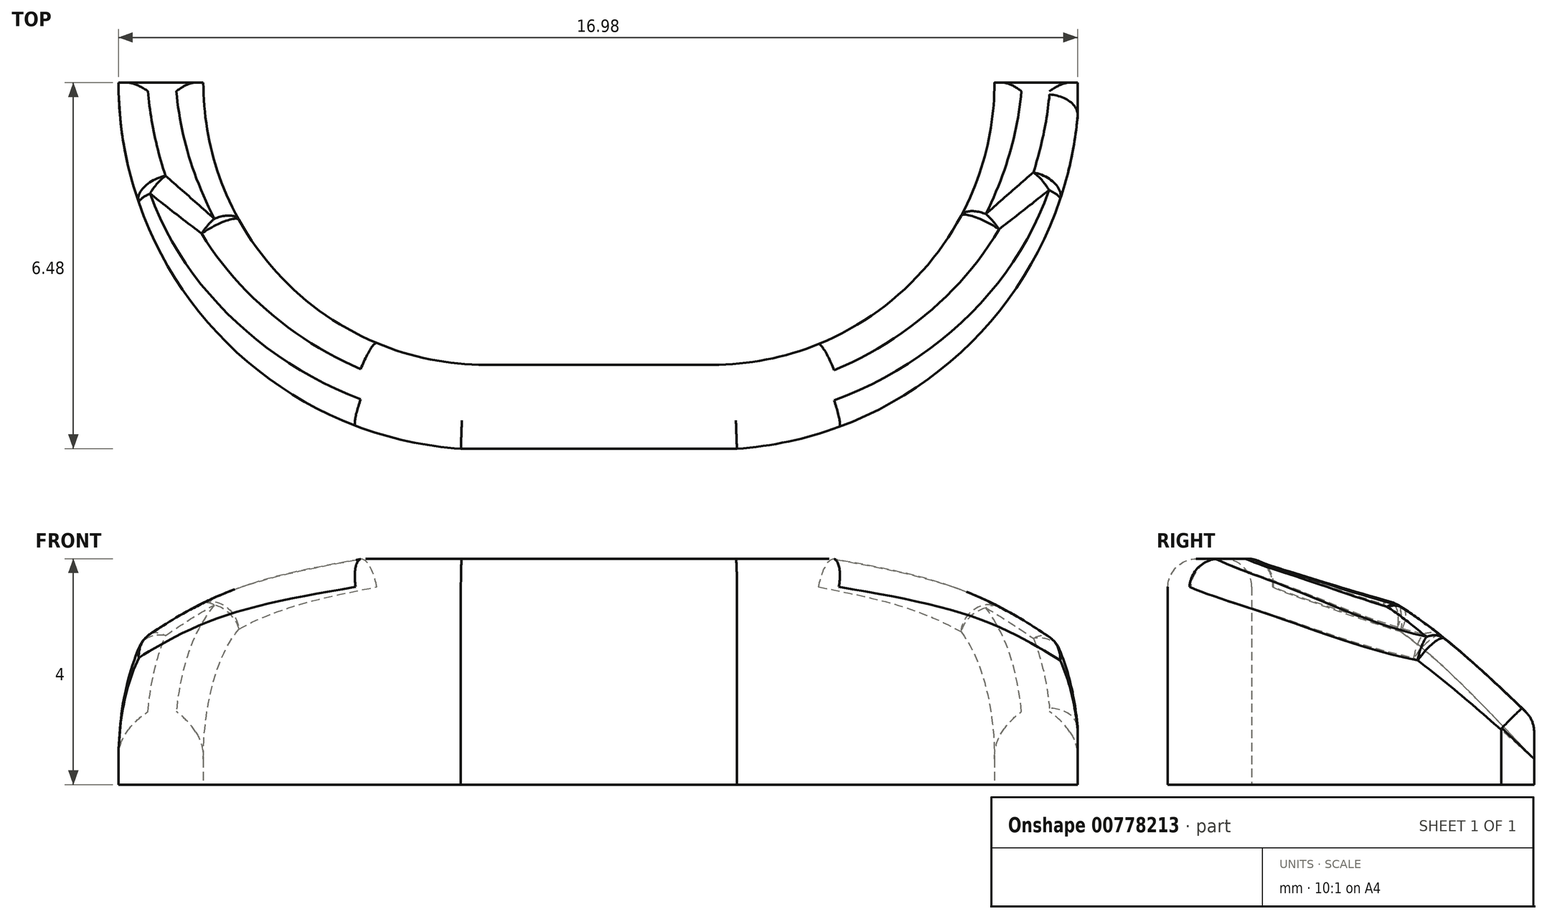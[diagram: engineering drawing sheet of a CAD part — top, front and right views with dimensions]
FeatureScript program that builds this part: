
annotation { "Feature Type Name" : "Feature", "Feature Type Description" : "" }
export const myFeature = defineFeature(function(context is Context, id is Id, definition is map)
    precondition{}
    {
        {
            var Q0;
            Q0=qCreatedBy(makeId("Top.planeOp"),FACE);
            var sketch = newSketch(context, id + "F0", { "sketchPlane" : qUnion([Q0])});
            skLineSegment(sketch, "E0", {"start": v(1.74, -7.18) * mm, "end": v(5.74, -7.18) * mm});
            skPoint(sketch, "E1.visualSharp", {"position": v(-3.26, -7.18) * mm});
            skArc(sketch, "E1.filletArc", {"start": v(-3.26, -2.18) * mm, "mid": v(-1.8, -5.72) * mm, "end": v(1.74, -7.18) * mm});
            skPoint(sketch, "E2.visualSharp", {"position": v(10.74, -7.18) * mm});
            skArc(sketch, "E2.filletArc", {"start": v(5.74, -7.18) * mm, "mid": v(9.28, -5.72) * mm, "end": v(10.74, -2.18) * mm});
            skArc(sketch, "E3.0", {"start": v(-4.76, -2.18) * mm, "mid": v(-2.86, -6.78) * mm, "end": v(1.74, -8.68) * mm});
            skArc(sketch, "E4.0", {"start": v(5.74, -8.68) * mm, "mid": v(10.34, -6.78) * mm, "end": v(12.24, -2.18) * mm});
            skLineSegment(sketch, "E5", {"start": v(1.74, -8.68) * mm, "end": v(5.74, -8.68) * mm});
            skLineSegment(sketch, "E6", {"start": v(-4.76, -2.18) * mm, "end": v(-3.26, -2.18) * mm});
            skLineSegment(sketch, "E7", {"start": v(10.74, -2.18) * mm, "end": v(12.24, -2.18) * mm});
            skPoint(sketch, "E8.start.orphan", {"position": v(-3.26, 0.61) * mm});
            skPoint(sketch, "E9.end.orphan", {"position": v(10.74, 0.61) * mm});
            skLineSegment(sketch, "E10", {"start": v(-4.76, -2.18) * mm, "end": v(-4.76, -8.68) * mm});
            skLineSegment(sketch, "E11", {"start": v(-4.76, -8.68) * mm, "end": v(12.24, -8.68) * mm});
            skLineSegment(sketch, "E12", {"start": v(12.24, -8.68) * mm, "end": v(12.24, -2.18) * mm});
            skLineSegment(sketch, "E13", {"start": v(12.24, -2.18) * mm, "end": v(-4.76, -2.18) * mm});
            skSolve(sketch);
        }
        {
            var Q0;
            Q0=makeQuery(id+"F0.imprint","IMPRINT",FACE,{"disambiguationData":[TD([[makeQuery(id+"F0.imprint","IMPRINT",EDGE,{"derivedFrom":sQuery(id+"F0.wireOp",EDGE,"E0")}),-1.0]])]});
            var Q1;
            Q1=makeQuery(id+"F0.imprint","IMPRINT",FACE,{"disambiguationData":[TD([[makeQuery(id+"F0.imprint","IMPRINT",EDGE,{"derivedFrom":sQuery(id+"F0.wireOp",EDGE,"E0")}),1.0]])]});
            var Q2;
            {var subQ0=sQuery(id+"F0.wireOp",EDGE,"E4.0");Q2=makeQuery(id+"F0.imprint","IMPRINT",FACE,{"disambiguationData":[TD([[makeQuery(id+"F0.imprint","IMPRINT",EDGE,{"derivedFrom":subQ0}),-1.0]])]});}
            var Q3;
            {var subQ0=sQuery(id+"F0.wireOp",EDGE,"E3.0");Q3=makeQuery(id+"F0.imprint","IMPRINT",FACE,{"disambiguationData":[TD([[makeQuery(id+"F0.imprint","IMPRINT",EDGE,{"derivedFrom":subQ0}),-1.0]])]});}
            extrude(context, id + "F1", {"entities" : qUnion([Q0, Q1, Q2, Q3]), "depth" : 4 * mm, "offsetDistance" : 25 * mm});
        }
        {
            var Q0;
            Q0=makeQuery(id+"F1.opExtrude","SWEPT_FACE",FACE,{"disambiguationData":[OSD([sQuery(id+"F0.wireOp",EDGE,"E12")])]});
            var sketch = newSketch(context, id + "F2", { "sketchPlane" : qUnion([Q0])});
            skFitSpline(sketch, "E14", {"points": [v(-6.61, 4) * mm, v(-4.66, 3.21) * mm, v(-2.18, 1.13) * mm], "startDerivative": vector(4.34, -1.32) * mm, "endDerivative": vector(4.51, -4.31) * mm});
            skSolve(sketch);
        }
        {
            var Q0;
            {var subQ0=sQuery(id+"F2.wireOp",EDGE,"E14");Q0=makeQuery(id+"F2.imprint","IMPRINT",FACE,{"disambiguationData":[TD([[makeQuery(id+"F2.imprint","IMPRINT",EDGE,{"derivedFrom":subQ0}),1.0]])]});}
            extrude(context, id + "F3", {"entities" : qUnion([Q0]), "operationType" : NewBodyOperationType.REMOVE, "endBound" : BoundingType.THROUGH_ALL, "oppositeDirection" : true, "depth" : 25 * mm, "offsetDistance" : 25 * mm});
        }
        {
            var Q0;
            Q0=makeQuery(id+"F1.opExtrude","SWEPT_FACE",FACE,{"disambiguationData":[OSD([sQuery(id+"F0.wireOp",EDGE,"E11")])]});
            var sketch = newSketch(context, id + "F4", { "sketchPlane" : qUnion([Q0])});
            skLineSegment(sketch, "E15", {"start": v(3.74, 4) * mm, "end": v(3.74, 0) * mm, "construction": true});
            skFitSpline(sketch, "E16", {"points": [v(-0.4, 4) * mm, v(-2.85, 3.4) * mm, v(-4.76, 2.27) * mm], "startDerivative": vector(-4.94, -0.89) * mm, "endDerivative": vector(-3.76, -2.59) * mm});
            skFitSpline(sketch, "E17.MirrorCS", {"points": [v(7.89, 4) * mm, v(10.33, 3.4) * mm, v(12.24, 2.27) * mm], "startDerivative": vector(4.94, -0.89) * mm, "endDerivative": vector(3.76, -2.59) * mm});
            skSolve(sketch);
        }
        {
            var Q0;
            {var subQ0=sQuery(id+"F4.wireOp",EDGE,"E16");Q0=makeQuery(id+"F4.imprint","IMPRINT",FACE,{"disambiguationData":[TD([[makeQuery(id+"F4.imprint","IMPRINT",EDGE,{"derivedFrom":subQ0}),-1.0]])]});}
            var Q1;
            {var subQ0=sQuery(id+"F4.wireOp",EDGE,"E17.MirrorCS");Q1=makeQuery(id+"F4.imprint","IMPRINT",FACE,{"disambiguationData":[TD([[makeQuery(id+"F4.imprint","IMPRINT",EDGE,{"derivedFrom":subQ0}),1.0]])]});}
            extrude(context, id + "F5", {"entities" : qUnion([Q0, Q1]), "operationType" : NewBodyOperationType.REMOVE, "endBound" : BoundingType.THROUGH_ALL, "oppositeDirection" : true, "depth" : 25 * mm, "offsetDistance" : 25 * mm});
        }
        {
            var Q0;
            Q0=makeQuery(id+"F1.opExtrude","CAP_FACE",FACE,{"disambiguationData":[OSD([sQuery(id+"F0.wireOp",EDGE,"E10"),sQuery(id+"F0.wireOp",EDGE,"E11"),sQuery(id+"F0.wireOp",EDGE,"E12"),sQuery(id+"F0.wireOp",EDGE,"E13")])],"isStart":true});
            var sketch = newSketch(context, id + "F6", { "sketchPlane" : qUnion([Q0])});
            skLineSegment(sketch, "E18", {"start": v(5.77, 7.2) * mm, "end": v(1.76, 7.2) * mm});
            skPoint(sketch, "E19.visualSharp", {"position": v(10.77, 7.2) * mm});
            skArc(sketch, "E19.filletArc", {"start": v(10.77, 2.2) * mm, "mid": v(9.3, 5.73) * mm, "end": v(5.77, 7.2) * mm});
            skPoint(sketch, "E20.visualSharp", {"position": v(-3.24, 7.2) * mm});
            skArc(sketch, "E20.filletArc", {"start": v(1.76, 7.2) * mm, "mid": v(-1.77, 5.73) * mm, "end": v(-3.24, 2.2) * mm});
            skArc(sketch, "E21.0", {"start": v(12.27, 2.2) * mm, "mid": v(10.36, 6.8) * mm, "end": v(5.77, 8.7) * mm});
            skArc(sketch, "E22.0", {"start": v(1.76, 8.7) * mm, "mid": v(-2.83, 6.8) * mm, "end": v(-4.74, 2.2) * mm});
            skLineSegment(sketch, "E23", {"start": v(5.77, 8.7) * mm, "end": v(1.76, 8.7) * mm});
            skLineSegment(sketch, "E24", {"start": v(12.27, 2.2) * mm, "end": v(10.77, 2.2) * mm});
            skLineSegment(sketch, "E25", {"start": v(-3.24, 2.2) * mm, "end": v(-4.74, 2.2) * mm});
            skSolve(sketch);
        }
        {
            var Q0;
            {var subQ0=sQuery(id+"F6.wireOp",EDGE,"E21.0");var subQ1=makeQuery(id+"F1.opExtrude","CAP_EDGE",EDGE,{"disambiguationData":[OSD([sQuery(id+"F0.wireOp",EDGE,"E12")])],"isStart":true});var subQ2=makeQuery(id+"F6.imprint","INTERSECT",VERTEX,{"derivedFrom":[subQ1,subQ0]});Q0=makeQuery(id+"F6.imprint","IMPRINT",FACE,{"disambiguationData":[TD([[makeQuery(id+"F6.imprint","IMPRINT",EDGE,{"disambiguationData":[TD([[subQ2,-1.0]])],"derivedFrom":subQ0}),-1.0]])]});}
            var Q1;
            Q1=makeQuery(id+"F6.imprint","IMPRINT",FACE,{"disambiguationData":[TD([[makeQuery(id+"F6.imprint","IMPRINT",EDGE,{"derivedFrom":sQuery(id+"F6.wireOp",EDGE,"E18")}),1.0]])]});
            extrude(context, id + "F7", {"entities" : qUnion([Q0, Q1]), "operationType" : NewBodyOperationType.REMOVE, "endBound" : BoundingType.THROUGH_ALL, "oppositeDirection" : true, "depth" : 25 * mm, "offsetDistance" : 25 * mm});
        }
        {
            var Q0;
            Q0=makeQuery(id+"F7.boolean.opBoolean","SPLIT",FACE,{"disambiguationData":[TD([makeQuery(id+"F5.boolean.opBoolean","COPY",FACE,{"derivedFrom":makeQuery(id+"F5.opExtrude","SWEPT_FACE",FACE,{"disambiguationData":[OSD([sQuery(id+"F4.wireOp",EDGE,"E16")])]})})])],"derivedFrom":makeQuery(id+"F3.boolean.opBoolean","COPY",FACE,{"derivedFrom":makeQuery(id+"F3.opExtrude","SWEPT_FACE",FACE,{"disambiguationData":[OSD([sQuery(id+"F2.wireOp",EDGE,"E14")])]})})});
            var Q1;
            Q1=makeQuery(id+"F7.boolean.opBoolean","SPLIT",FACE,{"disambiguationData":[TD([makeQuery(id+"F1.opExtrude","SWEPT_FACE",FACE,{"disambiguationData":[OSD([sQuery(id+"F0.wireOp",EDGE,"E12")])]})])],"derivedFrom":makeQuery(id+"F3.boolean.opBoolean","COPY",FACE,{"derivedFrom":makeQuery(id+"F3.opExtrude","SWEPT_FACE",FACE,{"disambiguationData":[OSD([sQuery(id+"F2.wireOp",EDGE,"E14")])]})})});
            var Q2;
            Q2=makeQuery(id+"F5.boolean.opBoolean","COPY",FACE,{"derivedFrom":makeQuery(id+"F5.opExtrude","SWEPT_FACE",FACE,{"disambiguationData":[OSD([sQuery(id+"F4.wireOp",EDGE,"E17.MirrorCS")])]})});
            var Q3;
            Q3=makeQuery(id+"F1.opExtrude","CAP_FACE",FACE,{"disambiguationData":[OSD([sQuery(id+"F0.wireOp",EDGE,"E10"),sQuery(id+"F0.wireOp",EDGE,"E11"),sQuery(id+"F0.wireOp",EDGE,"E12"),sQuery(id+"F0.wireOp",EDGE,"E13")])],"isStart":false});
            var Q4;
            Q4=makeQuery(id+"F5.boolean.opBoolean","COPY",FACE,{"derivedFrom":makeQuery(id+"F5.opExtrude","SWEPT_FACE",FACE,{"disambiguationData":[OSD([sQuery(id+"F4.wireOp",EDGE,"E16")])]})});
            fillet(context, id + "F8", {"entities" : qUnion([Q0, Q1, Q2, Q3, Q4]), "radius" : .5 * mm, "tangentPropagation" : true, "allowEdgeOverflow" : false});
        }
    });
